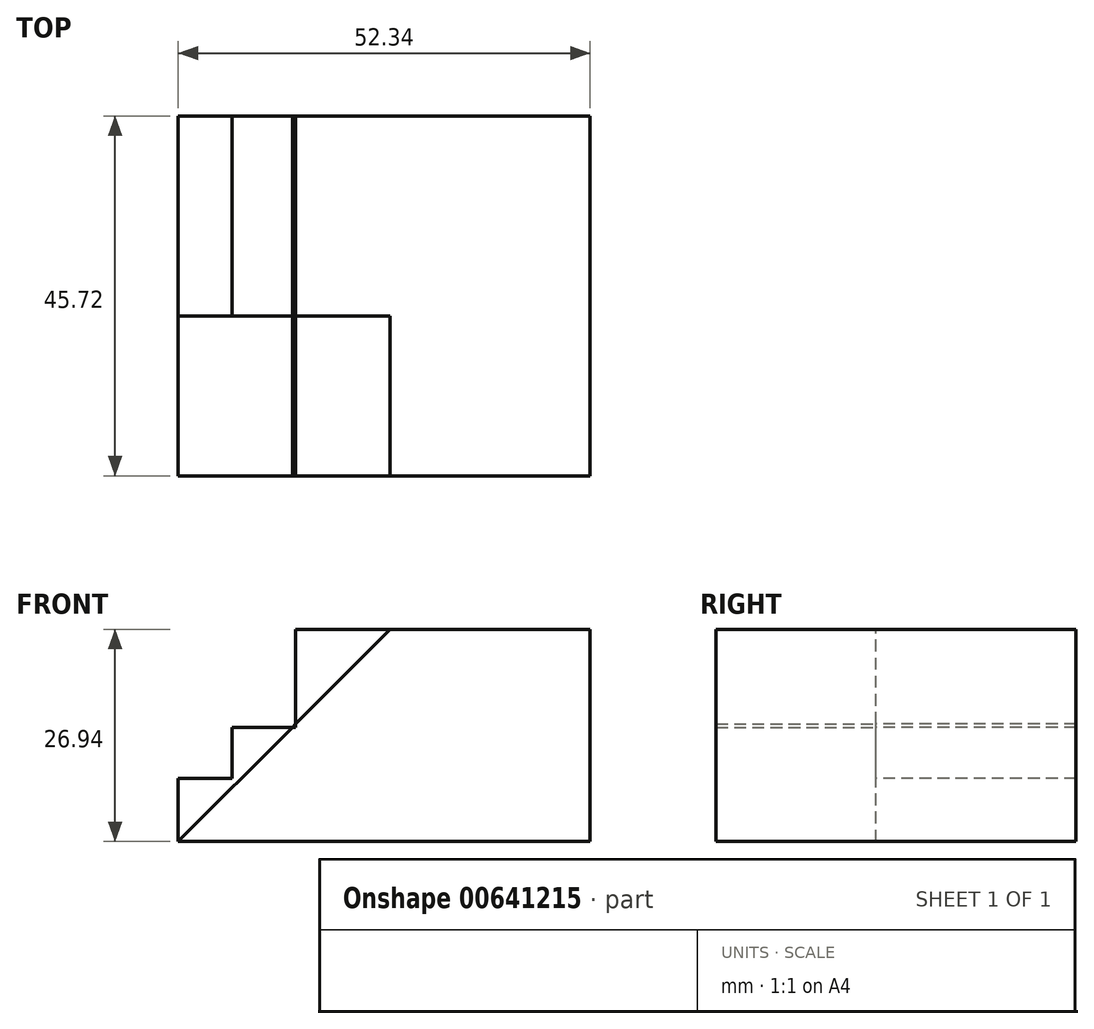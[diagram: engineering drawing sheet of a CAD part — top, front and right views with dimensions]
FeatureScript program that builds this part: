
annotation { "Feature Type Name" : "Feature", "Feature Type Description" : "" }
export const myFeature = defineFeature(function(context is Context, id is Id, definition is map)
    precondition{}
    {
        {
            var Q0;
            Q0=qCreatedBy(makeId("Front.planeOp"),FACE);
            var sketch = newSketch(context, id + "F0", { "sketchPlane" : qUnion([Q0])});
            skLineSegment(sketch, "E0", {"start": v(0, 0) * mm, "end": v(0, 8.01) * mm});
            skLineSegment(sketch, "E1", {"start": v(0, 8.01) * mm, "end": v(6.86, 8.01) * mm});
            skLineSegment(sketch, "E2", {"start": v(6.86, 8.01) * mm, "end": v(6.86, 14.5) * mm});
            skLineSegment(sketch, "E3", {"start": v(6.86, 14.5) * mm, "end": v(14.94, 14.5) * mm});
            skLineSegment(sketch, "E4", {"start": v(14.94, 14.5) * mm, "end": v(14.94, 26.94) * mm});
            skLineSegment(sketch, "E5", {"start": v(14.94, 26.94) * mm, "end": v(26.94, 26.94) * mm});
            skLineSegment(sketch, "E6", {"start": v(26.94, 26.94) * mm, "end": v(26.94, 0) * mm});
            skLineSegment(sketch, "E7", {"start": v(26.94, 0) * mm, "end": v(0, 0) * mm});
            skLineSegment(sketch, "E8", {"start": v(0, 0) * mm, "end": v(26.94, 26.94) * mm});
            skSolve(sketch);
        }
        {
            var Q0;
            Q0=makeQuery(id+"F0.imprint","IMPRINT",FACE,{"disambiguationData":[TD([[makeQuery(id+"F0.imprint","IMPRINT",EDGE,{"derivedFrom":sQuery(id+"F0.wireOp",EDGE,"E6")}),-1.0]])]});
            extrude(context, id + "F1", {"entities" : qUnion([Q0]), "depth" : 20.32 * mm, "offsetDistance" : 25.4 * mm});
        }
        {
            var Q0;
            Q0 = qSketchRegion(id + "F0", true);
            extrude(context, id + "F2", {"entities" : qUnion([Q0]), "operationType" : NewBodyOperationType.ADD, "oppositeDirection" : true, "depth" : 25.4 * mm, "offsetDistance" : 25.4 * mm});
        }
        {
            var Q0;
            {var subQ0=sQuery(id+"F0.wireOp",EDGE,"E6");Q0=makeQuery(id+"F2.boolean.opBoolean","MERGE",FACE,{"derivedFrom":[makeQuery(id+"F1.opExtrude","SWEPT_FACE",FACE,{"disambiguationData":[OSD([subQ0])]}),makeQuery(id+"F2.opExtrude","SWEPT_FACE",FACE,{"disambiguationData":[OSD([subQ0])]})]});}
            extrude(context, id + "F3", {"entities" : qUnion([Q0]), "operationType" : NewBodyOperationType.ADD, "depth" : 25.4 * mm, "offsetDistance" : 25.4 * mm});
        }
    });
